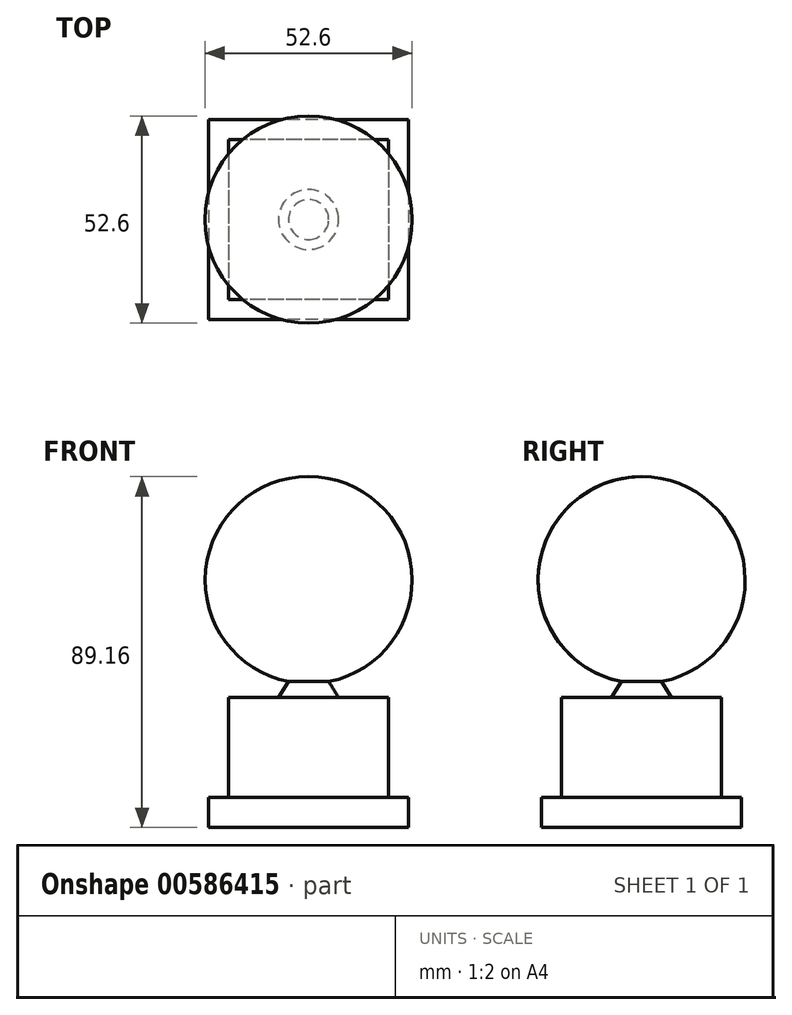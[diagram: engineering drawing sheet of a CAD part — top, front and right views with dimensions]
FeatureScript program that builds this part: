
annotation { "Feature Type Name" : "Feature", "Feature Type Description" : "" }
export const myFeature = defineFeature(function(context is Context, id is Id, definition is map)
    precondition{}
    {
        {
            var Q0;
            Q0=qCreatedBy(makeId("Top.planeOp"),FACE);
            var sketch = newSketch(context, id + "F0", { "sketchPlane" : qUnion([Q0])});
            skLineSegment(sketch, "E0.bottom", {"start": v(25.4, 25.4) * mm, "end": v(-25.4, 25.4) * mm});
            skLineSegment(sketch, "E0.top", {"start": v(25.4, -25.4) * mm, "end": v(-25.4, -25.4) * mm});
            skLineSegment(sketch, "E0.left", {"start": v(25.4, 25.4) * mm, "end": v(25.4, -25.4) * mm});
            skLineSegment(sketch, "E0.right", {"start": v(-25.4, 25.4) * mm, "end": v(-25.4, -25.4) * mm});
            skPoint(sketch, "E0.middle", {"position": v(0, 0) * mm});
            skSolve(sketch);
        }
        {
            var Q0;
            Q0=makeQuery(id+"F0.imprint","IMPRINT",FACE,{"disambiguationData":[TD([[makeQuery(id+"F0.imprint","IMPRINT",EDGE,{"derivedFrom":sQuery(id+"F0.wireOp",EDGE,"E0.bottom")}),1.0]])]});
            extrude(context, id + "F1", {"entities" : qUnion([Q0]), "depth" : 7.62 * mm, "offsetDistance" : 25.4 * mm});
        }
        {
            var Q0;
            Q0=makeQuery(id+"F1.opExtrude","CAP_FACE",FACE,{"disambiguationData":[OSD([sQuery(id+"F0.wireOp",EDGE,"E0.bottom"),sQuery(id+"F0.wireOp",EDGE,"E0.top"),sQuery(id+"F0.wireOp",EDGE,"E0.left"),sQuery(id+"F0.wireOp",EDGE,"E0.right")])],"isStart":false});
            var sketch = newSketch(context, id + "F2", { "sketchPlane" : qUnion([Q0])});
            skLineSegment(sketch, "E1.bottom", {"start": v(20.32, 20.32) * mm, "end": v(-20.32, 20.32) * mm});
            skLineSegment(sketch, "E1.top", {"start": v(20.32, -20.32) * mm, "end": v(-20.32, -20.32) * mm});
            skLineSegment(sketch, "E1.left", {"start": v(20.32, 20.32) * mm, "end": v(20.32, -20.32) * mm});
            skLineSegment(sketch, "E1.right", {"start": v(-20.32, 20.32) * mm, "end": v(-20.32, -20.32) * mm});
            skPoint(sketch, "E1.middle", {"position": v(0, 0) * mm});
            skSolve(sketch);
        }
        {
            var Q0;
            Q0=makeQuery(id+"F2.imprint","IMPRINT",FACE,{"disambiguationData":[TD([[makeQuery(id+"F2.imprint","IMPRINT",EDGE,{"derivedFrom":sQuery(id+"F2.wireOp",EDGE,"E1.bottom")}),1.0]])]});
            extrude(context, id + "F3", {"entities" : qUnion([Q0]), "operationType" : NewBodyOperationType.ADD, "depth" : 25.4 * mm, "offsetDistance" : 25.4 * mm});
        }
        {
            var Q0;
            Q0=makeQuery(id+"F3.opExtrude","CAP_FACE",FACE,{"disambiguationData":[OSD([sQuery(id+"F2.wireOp",EDGE,"E1.bottom"),sQuery(id+"F2.wireOp",EDGE,"E1.top"),sQuery(id+"F2.wireOp",EDGE,"E1.left"),sQuery(id+"F2.wireOp",EDGE,"E1.right")])],"isStart":false});
            var sketch = newSketch(context, id + "F4", { "sketchPlane" : qUnion([Q0])});
            skCircle(sketch, "E2", {"center": v(0, 0) * mm, "radius": 7.62 * mm});
            skSolve(sketch);
        }
        {
            var Q0;
            Q0=makeQuery(id+"F4.imprint","IMPRINT",FACE,{"disambiguationData":[TD([[makeQuery(id+"F4.imprint","IMPRINT",EDGE,{"derivedFrom":sQuery(id+"F4.wireOp",EDGE,"E2")}),-1.0]])]});
            cPlane(context, id + "F5", {"entities" : qUnion([Q0]), "cplaneType" : CPlaneType.OFFSET, "offset" : 5.08 * mm, "width" : 152.4 * mm, "height" : 152.4 * mm});
        }
        {
            var Q0;
            Q0=qCreatedBy(id+"F5.planeOp",FACE);
            var sketch = newSketch(context, id + "F6", { "sketchPlane" : qUnion([Q0])});
            skCircle(sketch, "E3", {"center": v(0, 0) * mm, "radius": 4.44 * mm});
            skSolve(sketch);
        }
        {
            var Q1;
            Q1=makeQuery(id+"F4.imprint","IMPRINT",FACE,{"disambiguationData":[TD([[makeQuery(id+"F4.imprint","IMPRINT",EDGE,{"derivedFrom":sQuery(id+"F4.wireOp",EDGE,"E2")}),1.0]])]});
            var Q2;
            Q2=makeQuery(id+"F6.imprint","IMPRINT",FACE,{"disambiguationData":[TD([[makeQuery(id+"F6.imprint","IMPRINT",EDGE,{"derivedFrom":sQuery(id+"F6.wireOp",EDGE,"E3")}),1.0]])]});
            loft(context, id + "F7", {"operationType" : NewBodyOperationType.ADD, "sheetProfilesArray" : [{ "sheetProfileEntities" : qUnion([Q1]) }, { "sheetProfileEntities" : qUnion([Q2]) }]});
        }
        {
            var Q0;
            Q0=makeQuery(id+"F3.opExtrude","SWEPT_FACE",FACE,{"disambiguationData":[OSD([sQuery(id+"F2.wireOp",EDGE,"E1.left")])]});
            cPlane(context, id + "F8", {"entities" : qUnion([Q0]), "cplaneType" : CPlaneType.OFFSET, "offset" : 20.32 * mm, "oppositeDirection" : true, "width" : 152.4 * mm, "height" : 152.4 * mm});
        }
        {
            var Q0;
            Q0=qCreatedBy(id+"F8.planeOp",FACE);
            var sketch = newSketch(context, id + "F9", { "sketchPlane" : qUnion([Q0])});
            skArc(sketch, "E4", {"start": v(0, 36.55) * mm, "mid": v(26.3, 62.85) * mm, "end": v(0, 89.16) * mm});
            skPoint(sketch, "E5.center.orphan", {"position": v(0, 56.75) * mm});
            skPoint(sketch, "E6.trimOffspring.end.orphan", {"position": v(0, 88.25) * mm});
            skPoint(sketch, "E6.trimOffspring.start.orphan", {"position": v(0, 76.04) * mm});
            skPoint(sketch, "E7.orphan", {"position": v(0, 37.45) * mm});
            skLineSegment(sketch, "E8", {"start": v(0, 37.45) * mm, "end": v(0, 88.25) * mm});
            skLineSegment(sketch, "E9", {"start": v(0, 89.16) * mm, "end": v(0, 36.55) * mm});
            skSolve(sketch);
        }
        {
            var Q0;
            {var subQ0=sQuery(id+"F9.wireOp",EDGE,"E4");Q0=makeQuery(id+"F9.imprint","IMPRINT",FACE,{"disambiguationData":[TD([[makeQuery(id+"F9.imprint","IMPRINT",EDGE,{"derivedFrom":subQ0}),1.0]])]});}
            var Q1;
            Q1=sQuery(id+"F9.wireOp",EDGE,"E9");
            revolve(context, id + "F10", {"operationType" : NewBodyOperationType.ADD, "entities" : qUnion([Q0]), "axis" : qUnion([Q1]), "revolveType" : RevolveType.FULL});
        }
    });
